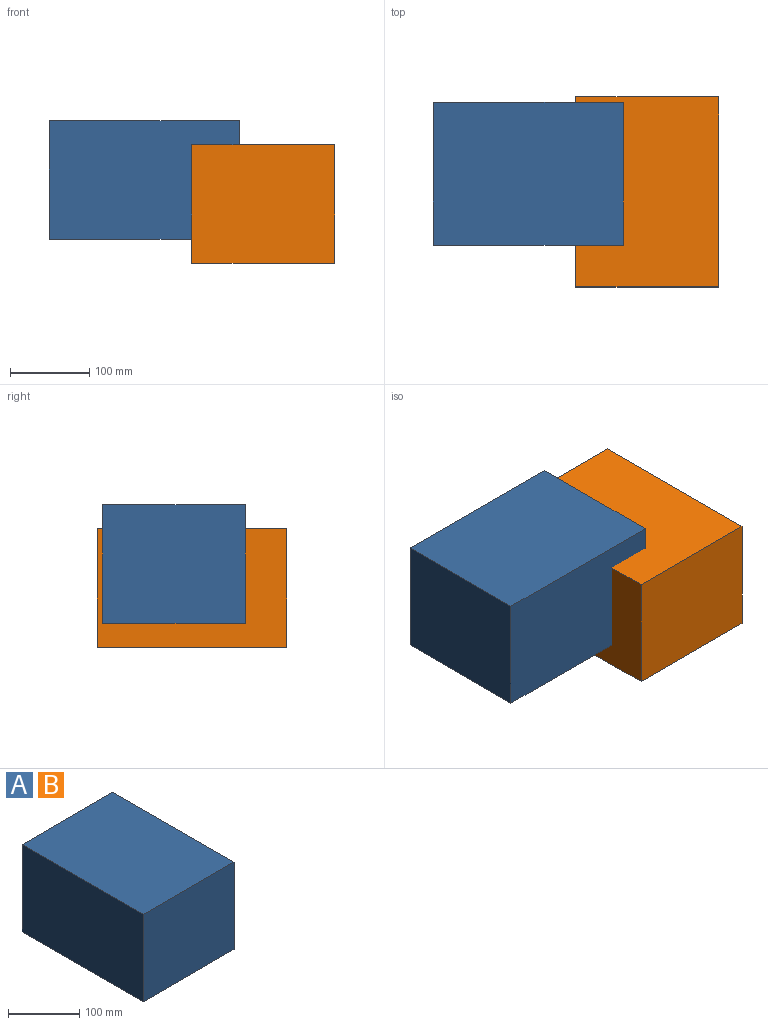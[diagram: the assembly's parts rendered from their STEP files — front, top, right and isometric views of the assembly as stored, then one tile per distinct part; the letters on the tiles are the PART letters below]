
ASSEMBLY  parts=2 mates=1
PART A: 6 faces, bbox 180.3x239.8x149.8 mm
  f0: plane 180.25x149.8mm, normal (0,1,0), area 27001.9mm2, adj f1,f3,f4,f5
  f1: plane 239.81x149.8mm, normal (-1,0,0), area 35923.5mm2, adj f0,f2,f4,f5
  f2: plane 180.25x149.8mm, normal (0,-1,0), area 27001.9mm2, adj f1,f3,f4,f5
  f3: plane 239.81x149.8mm, normal (1,0,0), area 35923.5mm2, adj f0,f2,f4,f5
  f4: plane 239.81x180.25mm, normal (0,0,-1), area 43226.5mm2, adj f0,f1,f2,f3
  f5: plane 239.81x180.25mm, normal (0,0,1), area 43226.5mm2, adj f0,f1,f2,f3
PART B: same geometry as A
PLACE A rot(axis=(0,0,-1),90deg) t=(42.11,29.89,15.18)mm
PLACE B t=(-18.01,36.93,-14.97)mm fixed
MATE parallel A.f2 <-> B.f3  axis (-1,0,0) through (-197.7,29.89,90.08)mm
